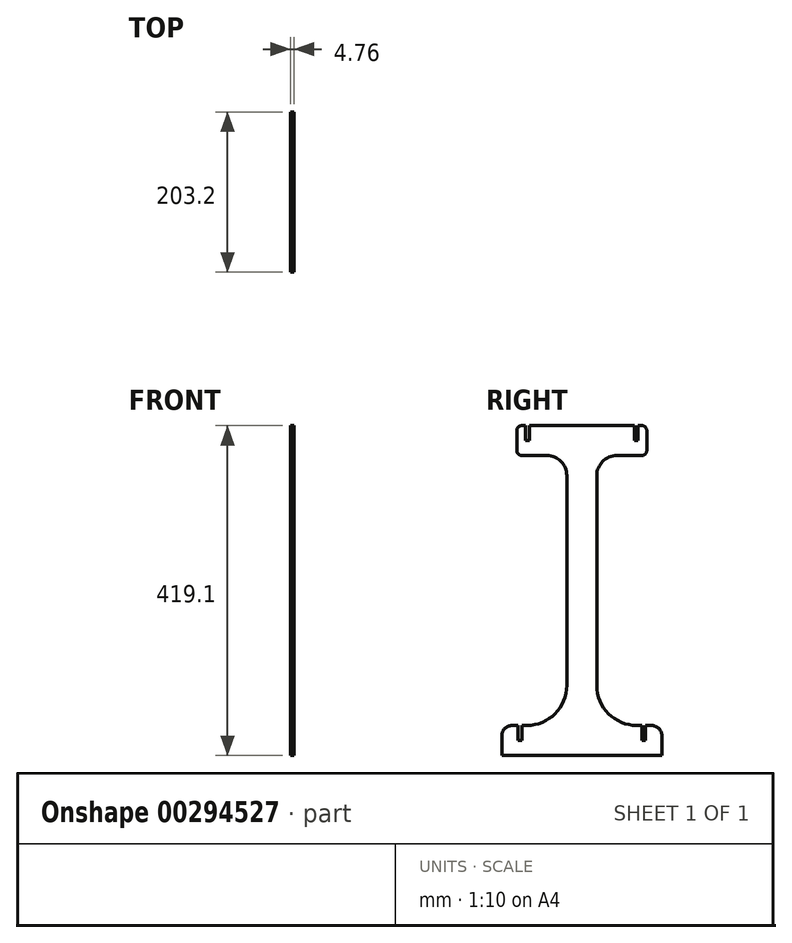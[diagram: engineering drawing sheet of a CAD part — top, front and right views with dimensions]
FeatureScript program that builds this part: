
annotation { "Feature Type Name" : "Feature", "Feature Type Description" : "" }
export const myFeature = defineFeature(function(context is Context, id is Id, definition is map)
    precondition{}
    {
        {
            var Q0;
            Q0=qCreatedBy(makeId("Right.planeOp"),FACE);
            var sketch = newSketch(context, id + "F0", { "sketchPlane" : qUnion([Q0])});
            skLineSegment(sketch, "E0.bottom", {"start": v(0, 0) * mm, "end": v(38.1, 0) * mm});
            skLineSegment(sketch, "E0.top", {"start": v(0, -419.1) * mm, "end": v(38.1, -419.1) * mm});
            skLineSegment(sketch, "E0.left", {"start": v(0, -63.5) * mm, "end": v(0, -330.2) * mm});
            skLineSegment(sketch, "E0.right", {"start": v(38.1, -63.5) * mm, "end": v(38.1, -330.2) * mm});
            skLineSegment(sketch, "E1.bottom", {"start": v(-57.15, 0) * mm, "end": v(-52.39, 0) * mm});
            skLineSegment(sketch, "E1.top", {"start": v(-57.15, -38.1) * mm, "end": v(-25.4, -38.1) * mm});
            skLineSegment(sketch, "E1.left", {"start": v(-63.5, -6.35) * mm, "end": v(-63.5, -31.75) * mm});
            skLineSegment(sketch, "E1.right", {"start": v(101.6, -6.35) * mm, "end": v(101.6, -31.75) * mm});
            skLineSegment(sketch, "E2", {"start": v(19.05, 0) * mm, "end": v(19.05, -38.1) * mm, "construction": true});
            skLineSegment(sketch, "E3.trimOffspring", {"start": v(63.5, -38.1) * mm, "end": v(95.25, -38.1) * mm});
            skPoint(sketch, "E4.visualSharp", {"position": v(101.6, -38.1) * mm});
            skArc(sketch, "E4.filletArc", {"start": v(95.25, -38.1) * mm, "mid": v(99.74, -36.24) * mm, "end": v(101.6, -31.75) * mm});
            skPoint(sketch, "E5.visualSharp", {"position": v(101.6, 0) * mm});
            skArc(sketch, "E5.filletArc", {"start": v(101.6, -6.35) * mm, "mid": v(99.74, -1.86) * mm, "end": v(95.25, 0) * mm});
            skPoint(sketch, "E6.visualSharp", {"position": v(-63.5, 0) * mm});
            skArc(sketch, "E6.filletArc", {"start": v(-57.15, 0) * mm, "mid": v(-61.64, -1.86) * mm, "end": v(-63.5, -6.35) * mm});
            skPoint(sketch, "E7.visualSharp", {"position": v(-63.5, -38.1) * mm});
            skArc(sketch, "E7.filletArc", {"start": v(-63.5, -31.75) * mm, "mid": v(-61.64, -36.24) * mm, "end": v(-57.15, -38.1) * mm});
            skLineSegment(sketch, "E8.top", {"start": v(-52.39, -19.05) * mm, "end": v(-47.63, -19.05) * mm});
            skLineSegment(sketch, "E8.left", {"start": v(-52.39, 0) * mm, "end": v(-52.39, -19.05) * mm});
            skLineSegment(sketch, "E8.right", {"start": v(-47.63, 0) * mm, "end": v(-47.63, -19.05) * mm});
            skLineSegment(sketch, "E9.MirrorCS", {"start": v(90.49, 0) * mm, "end": v(90.49, -19.05) * mm});
            skLineSegment(sketch, "E10.MirrorCS", {"start": v(90.49, -19.05) * mm, "end": v(85.72, -19.05) * mm});
            skLineSegment(sketch, "E11.MirrorCS", {"start": v(85.72, 0) * mm, "end": v(85.72, -19.05) * mm});
            skLineSegment(sketch, "E12.trimOffspring", {"start": v(-47.63, 0) * mm, "end": v(85.72, 0) * mm});
            skLineSegment(sketch, "E13.trimOffspring", {"start": v(90.49, 0) * mm, "end": v(95.25, 0) * mm});
            skPoint(sketch, "E14.visualSharp", {"position": v(0, -38.1) * mm});
            skArc(sketch, "E14.filletArc", {"start": v(0, -63.5) * mm, "mid": v(-7.44, -45.54) * mm, "end": v(-25.4, -38.1) * mm});
            skPoint(sketch, "E15.visualSharp", {"position": v(38.1, -38.1) * mm});
            skArc(sketch, "E15.filletArc", {"start": v(63.5, -38.1) * mm, "mid": v(45.54, -45.54) * mm, "end": v(38.1, -63.5) * mm});
            skLineSegment(sketch, "E16.bottom", {"start": v(-82.55, -419.1) * mm, "end": v(0, -419.1) * mm});
            skLineSegment(sketch, "E16.top", {"start": v(-69.85, -381) * mm, "end": v(-61.91, -381) * mm});
            skLineSegment(sketch, "E16.left", {"start": v(-82.55, -419.1) * mm, "end": v(-82.55, -393.7) * mm});
            skLineSegment(sketch, "E16.right", {"start": v(120.65, -419.1) * mm, "end": v(120.65, -393.7) * mm});
            skLineSegment(sketch, "E17", {"start": v(19.05, -381) * mm, "end": v(19.05, -419.1) * mm, "construction": true});
            skLineSegment(sketch, "E18.trimOffspring", {"start": v(88.9, -381) * mm, "end": v(95.25, -381) * mm});
            skPoint(sketch, "E19.visualSharp", {"position": v(0, -381) * mm});
            skArc(sketch, "E19.filletArc", {"start": v(-50.8, -381) * mm, "mid": v(-14.88, -366.12) * mm, "end": v(0, -330.2) * mm});
            skPoint(sketch, "E20.visualSharp", {"position": v(38.1, -381) * mm});
            skArc(sketch, "E20.filletArc", {"start": v(38.1, -330.2) * mm, "mid": v(52.98, -366.12) * mm, "end": v(88.9, -381) * mm});
            skLineSegment(sketch, "E21.top", {"start": v(-61.91, -400.05) * mm, "end": v(-57.15, -400.05) * mm});
            skLineSegment(sketch, "E21.left", {"start": v(-61.91, -381) * mm, "end": v(-61.91, -400.05) * mm});
            skLineSegment(sketch, "E21.right", {"start": v(-57.15, -381) * mm, "end": v(-57.15, -400.05) * mm});
            skLineSegment(sketch, "E22.MirrorCS", {"start": v(100.01, -381) * mm, "end": v(100.01, -400.05) * mm});
            skLineSegment(sketch, "E23.MirrorCS", {"start": v(100.01, -400.05) * mm, "end": v(95.25, -400.05) * mm});
            skLineSegment(sketch, "E24.MirrorCS", {"start": v(95.25, -381) * mm, "end": v(95.25, -400.05) * mm});
            skPoint(sketch, "E25.visualSharp", {"position": v(-82.55, -381) * mm});
            skArc(sketch, "E25.filletArc", {"start": v(-69.85, -381) * mm, "mid": v(-78.83, -384.72) * mm, "end": v(-82.55, -393.7) * mm});
            skPoint(sketch, "E26.visualSharp", {"position": v(120.65, -381) * mm});
            skArc(sketch, "E26.filletArc", {"start": v(120.65, -393.7) * mm, "mid": v(116.93, -384.72) * mm, "end": v(107.95, -381) * mm});
            skLineSegment(sketch, "E27.trimOffspring", {"start": v(-57.15, -381) * mm, "end": v(-50.8, -381) * mm});
            skLineSegment(sketch, "E28.trimOffspring", {"start": v(100.01, -381) * mm, "end": v(107.95, -381) * mm});
            skLineSegment(sketch, "E29.trimOffspring", {"start": v(38.1, -419.1) * mm, "end": v(120.65, -419.1) * mm});
            skSolve(sketch);
        }
        {
            var Q0;
            Q0 = qSketchRegion(id + "F0", true);
            extrude(context, id + "F1", {"entities" : qUnion([Q0]), "depth" : 4.76 * mm});
        }
    });
